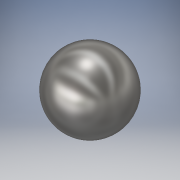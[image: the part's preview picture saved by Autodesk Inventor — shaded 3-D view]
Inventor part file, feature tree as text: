
AUTODESK INVENTOR PART (.ipt)
format: ipt  version: 2017 (Build 210142000, 142)  size: 126,976 bytes
history: native  units: in
note: dims shown in document units (in); Inventor stores cm internally (conversion verified against a paired STEP export)
features: revolve x1, sketch x1
ambient origin geometry x8: Origin, YZ Plane, XZ Plane, XY Plane, X Axis, Y Axis, Z Axis, Center Point
bodies: Solid1 (feature_tree)
feature tree (2):
  revolve  "Revolution1"  Angle=180.0deg
  sketch  "Sketch1"  dims[d0=0.25in d1=180.0deg]
